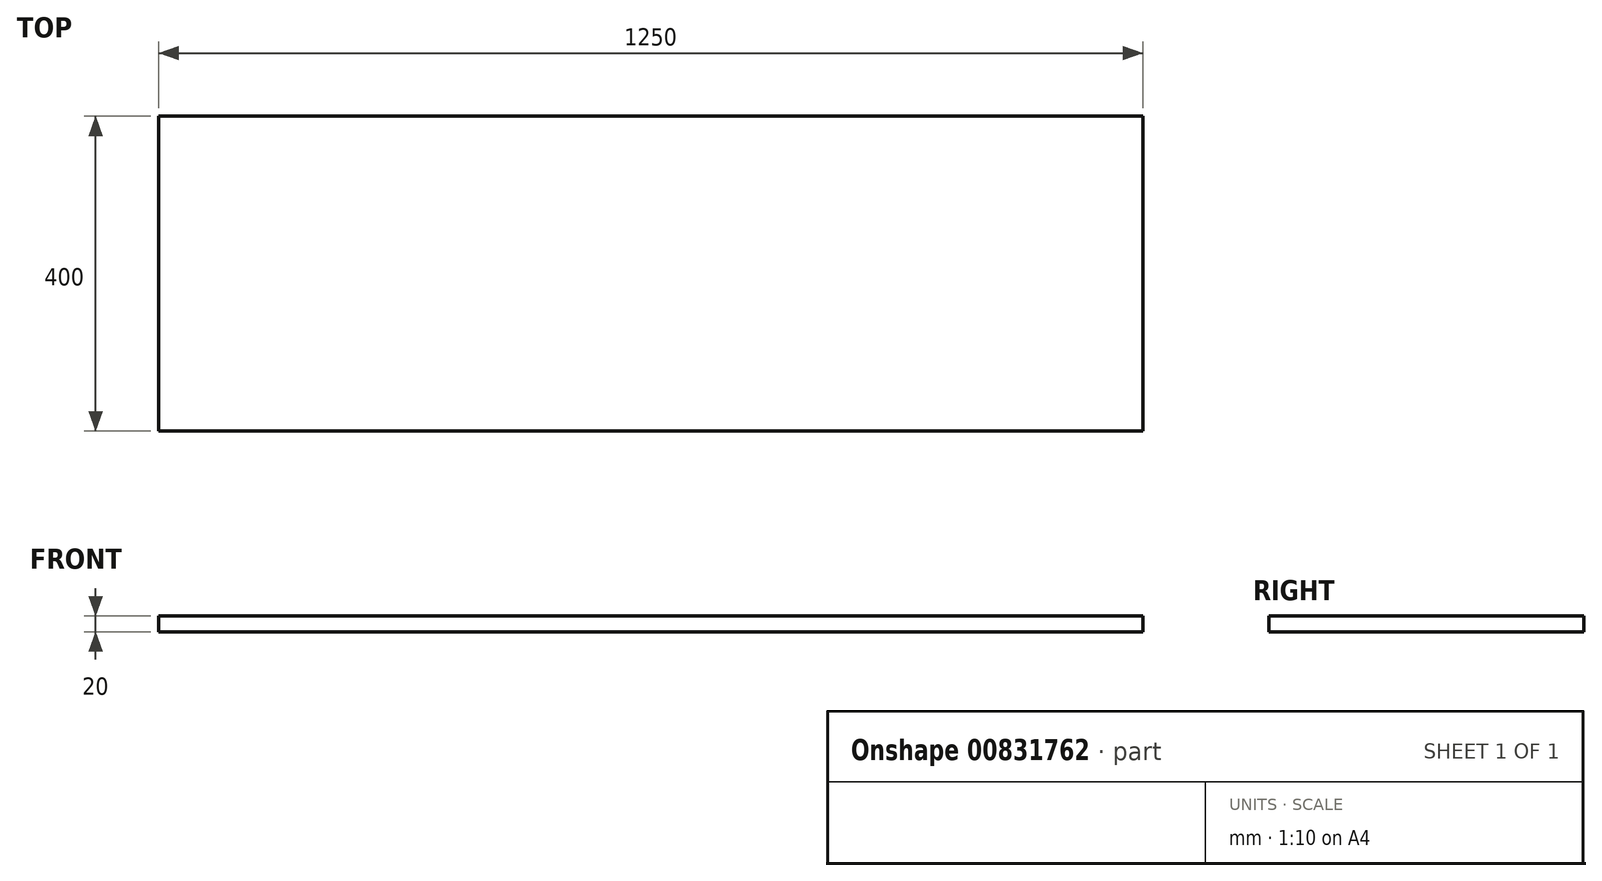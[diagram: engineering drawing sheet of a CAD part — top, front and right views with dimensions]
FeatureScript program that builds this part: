
annotation { "Feature Type Name" : "Feature", "Feature Type Description" : "" }
export const myFeature = defineFeature(function(context is Context, id is Id, definition is map)
    precondition{}
    {
        {
            var Q0;
            Q0=qCreatedBy(makeId("Front.planeOp"),FACE);
            var sketch = newSketch(context, id + "F0", { "sketchPlane" : qUnion([Q0])});
            skLineSegment(sketch, "E0.bottom", {"start": v(-32.9, 20) * mm, "end": v(1217.1, 20) * mm});
            skLineSegment(sketch, "E0.top", {"start": v(-32.9, 0) * mm, "end": v(1217.1, 0) * mm});
            skLineSegment(sketch, "E0.left", {"start": v(-32.9, 20) * mm, "end": v(-32.9, 0) * mm});
            skLineSegment(sketch, "E0.right", {"start": v(1217.1, 20) * mm, "end": v(1217.1, 0) * mm});
            skSolve(sketch);
        }
        {
            var Q0;
            Q0=makeQuery(id+"F0.imprint","IMPRINT",FACE,{"disambiguationData":[TD([[makeQuery(id+"F0.imprint","IMPRINT",EDGE,{"derivedFrom":sQuery(id+"F0.wireOp",EDGE,"E0.bottom")}),-1.0]])]});
            extrude(context, id + "F1", {"entities" : qUnion([Q0]), "depth" : 400 * mm, "offsetDistance" : 25 * mm});
        }
    });
